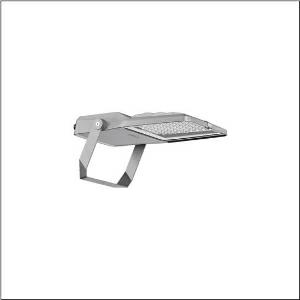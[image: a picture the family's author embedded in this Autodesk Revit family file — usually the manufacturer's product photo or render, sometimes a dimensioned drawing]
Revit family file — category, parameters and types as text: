
# Revit family: floodlight_fl_21_mini___pl52_5xa7772b5d1a_f50c
name_source: partatom
category: Lighting Fixtures
units: mm (PartAtom-declared; Revit-internal decimal feet)

## family parameters
Cut with Voids When Loaded = No
Host = Face
Light Source = No
Part Type = Normal
Room Calculation Point = No
Round Connector Dimension = Use Diameter
Shared = No

## types (1)
- --- (1 x LED, 5820 lm, 45.5 W, 4000K)
    Apparent Load = 46 VA
    CIE Flux Codes = 26 60 98 100 100
    Color Rendering = 80
    Color Temperature = 4000K
    Default Elevation = 1800 mm
    Description = Floodlight FL 21 mini, floodlight, primary light control with lens, of PMMA, primary optical cover: protective disc, of toughened safety glass, transparent, light distribution: PL52, light emission: direct distribution, installation type: surface-mounted, LED, High Power LED, rated luminous flux: 5.820lm, luminous efficacy: 128lm/W, light colour: 840, colour temperature: 4000K, control gear: ECG iQ, control: Street-Remote, Auto-Match, Temp-Guard, Night-Set, Smart-Wire, Desk-Remote (wireless, voltage-free reading and setting of iQ features in the workshop via application-optimized NFC function/RFID function), optimised constant luminous flux control (CLO 2.0), with terminal, 6-pole, mains connection: 220..240V, AC, 50/60Hz, start of lifetime: 46W, end of lifetime: 48W, reduction: 22W, luminaire housing, of diecast aluminium, powder-coated, Siteco® metallic grey (DB 702S), corrosivity category C5 according to DIN EN ISO 12944, mounting bracket, of steel, galvanised, powder-coated, Siteco® metallic grey (DB 702S), protection rating (complete): IP66, insulation class (complete): insulation class II (safety insulation), certification: CE, ENEC, VDE, protection symbol: D, impact resistance: IK08, permissible operating ambient temperature: -40..+40°C, permissible operating ambient temperature for outdoor applications: -40..+50°C, standard: DIN EN 12944, packaging unit: 1 piece

Light Distribution: PL52
    Height = 70 mm
    Lamp = 1 x LED
    Lamp Light Flux = 5820 lm
    Lamp Power = 45.5 W
    Lamp count = 1
    Length = 485 mm
    Luminous efficacy = 128 lm/W
    Manufacturer = Siteco
    ModVariant = No
    Model = 5XA7772B5D1A
    Number of Poles = 1
    OnlyDefault = Yes
    Power Factor = 1
    Product Name = Floodlight FL 21 mini | PL52
    Product group = floodlight | pylon top
    ProductGroupID = 6101
    Protection Class = Protection class II
    Protection Degree = IP 66
    RLX_Detail_Level = 1
    RlxData = <blob elided: 96337 chars, md5=563a185a>
    Socket = socket
    Standby Power = 0 W
    System Light Flux = 5820 lm
    System Power = 46 W
    Type Comments = factory setting: luminous flux: 100 % | dim-lin: 254 | 463 mA
    Type Image = l_1006845.jpg
    URL = http://relux.com
    VarID = @adj_075783
    Voltage = 0 V
    Weight = 0.00 kg
    Width = 337 mm

## geometry (parser evidence)
native form markers: Blend x4, Sweep x12
no freeform markers — native parametric forms only
